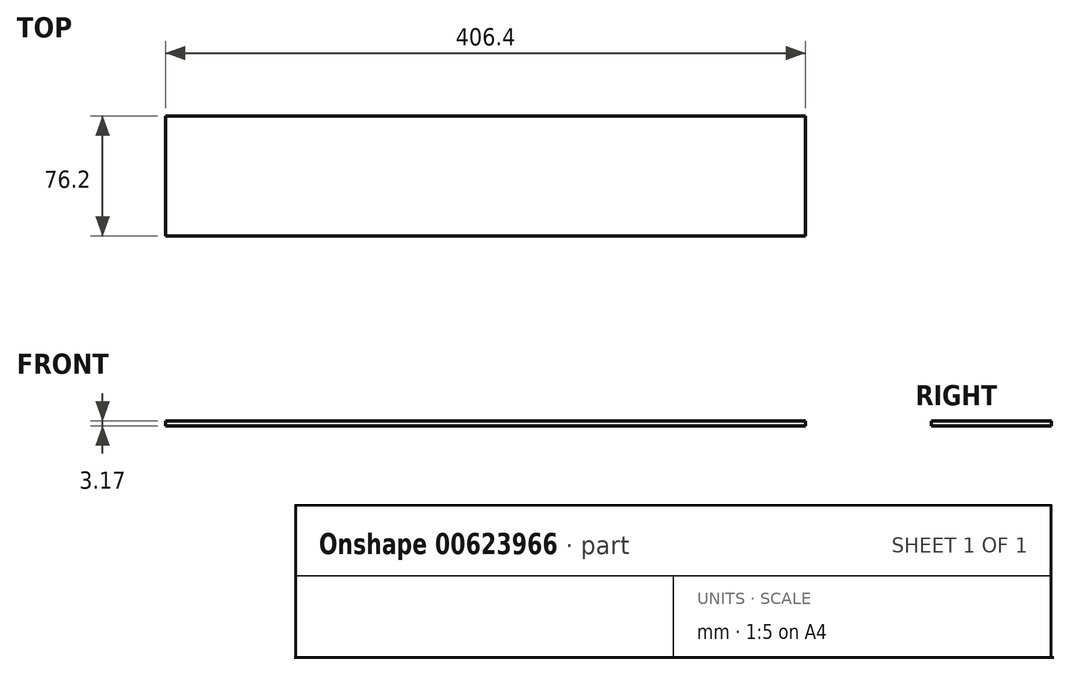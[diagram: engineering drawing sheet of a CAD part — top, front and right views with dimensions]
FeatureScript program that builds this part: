
annotation { "Feature Type Name" : "Feature", "Feature Type Description" : "" }
export const myFeature = defineFeature(function(context is Context, id is Id, definition is map)
    precondition{}
    {
        {
            var Q0;
            Q0=qCreatedBy(makeId("Top.planeOp"),FACE);
            var sketch = newSketch(context, id + "F0", { "sketchPlane" : qUnion([Q0])});
            skLineSegment(sketch, "E0.bottom", {"start": v(-212.73, -22.87) * mm, "end": v(193.67, -22.87) * mm});
            skLineSegment(sketch, "E0.top", {"start": v(-212.73, -99.07) * mm, "end": v(193.67, -99.07) * mm});
            skLineSegment(sketch, "E0.left", {"start": v(-212.73, -22.87) * mm, "end": v(-212.73, -99.07) * mm});
            skLineSegment(sketch, "E0.right", {"start": v(193.67, -22.87) * mm, "end": v(193.67, -99.07) * mm});
            skSolve(sketch);
        }
        {
            var Q0;
            Q0=makeQuery(id+"F0.imprint","IMPRINT",FACE,{"disambiguationData":[TD([[makeQuery(id+"F0.imprint","IMPRINT",EDGE,{"derivedFrom":sQuery(id+"F0.wireOp",EDGE,"E0.bottom")}),-1.0]])]});
            extrude(context, id + "F1", {"entities" : qUnion([Q0]), "depth" : 3.17 * mm, "offsetDistance" : 25.4 * mm});
        }
    });
